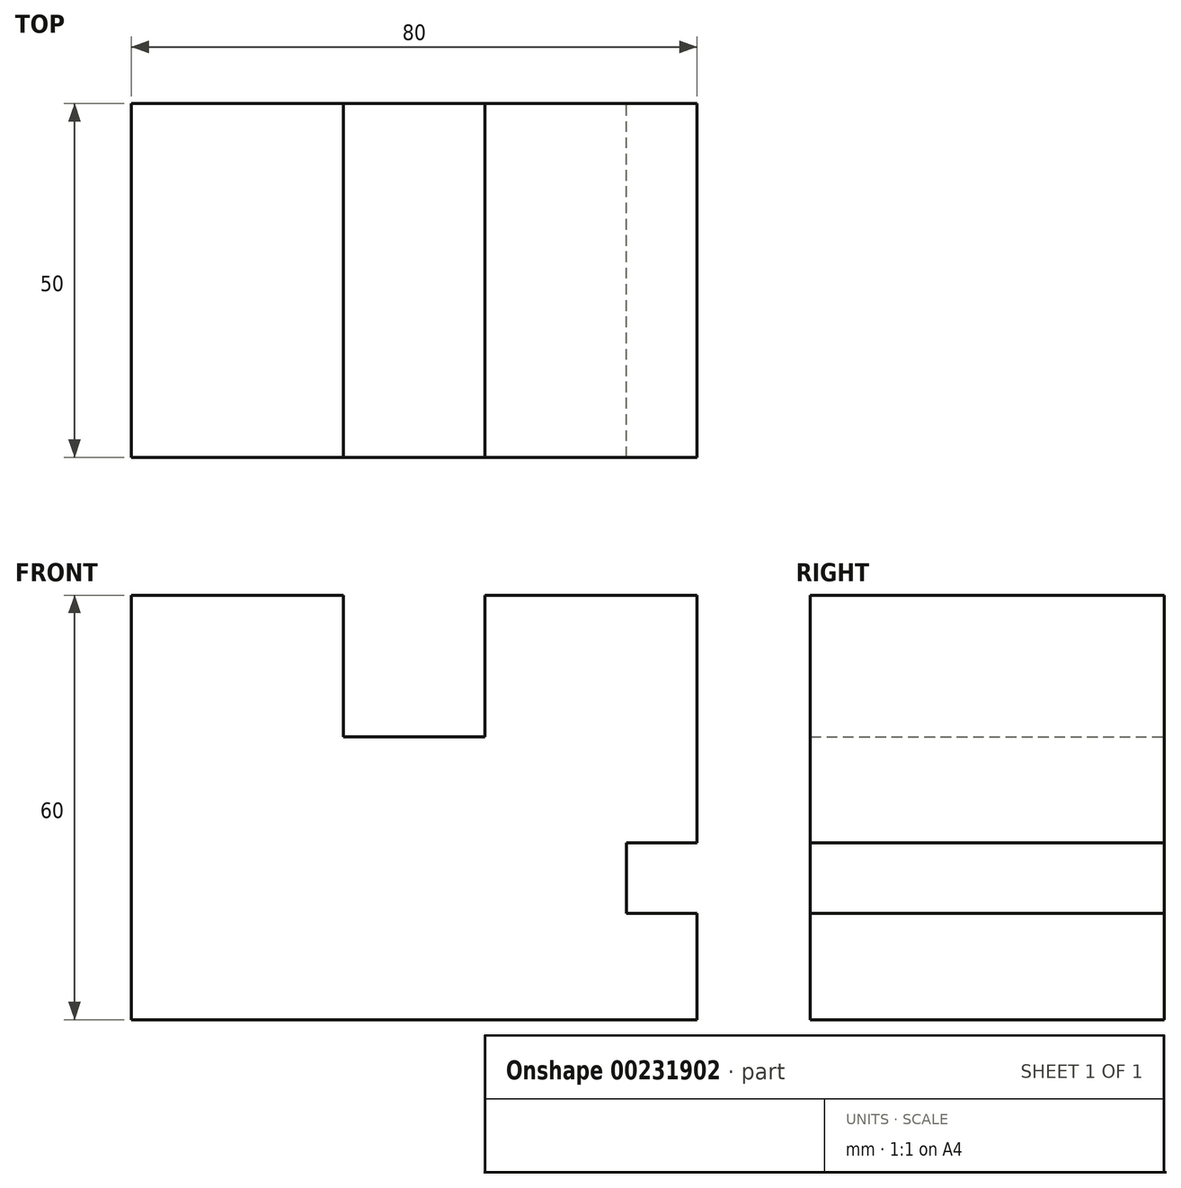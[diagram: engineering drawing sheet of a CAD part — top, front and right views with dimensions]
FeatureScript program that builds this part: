
annotation { "Feature Type Name" : "Feature", "Feature Type Description" : "" }
export const myFeature = defineFeature(function(context is Context, id is Id, definition is map)
    precondition{}
    {
        {
            var Q0;
            Q0=qCreatedBy(makeId("Front.planeOp"),FACE);
            var sketch = newSketch(context, id + "F0", { "sketchPlane" : qUnion([Q0])});
            skLineSegment(sketch, "E0", {"start": v(-80, 60) * mm, "end": v(-50, 60) * mm});
            skLineSegment(sketch, "E1", {"start": v(-50, 60) * mm, "end": v(-50, 40) * mm});
            skLineSegment(sketch, "E2", {"start": v(-50, 40) * mm, "end": v(-30, 40) * mm});
            skLineSegment(sketch, "E3", {"start": v(-30, 40) * mm, "end": v(-30, 60) * mm});
            skLineSegment(sketch, "E4", {"start": v(-30, 60) * mm, "end": v(0, 60) * mm});
            skLineSegment(sketch, "E5", {"start": v(0, 60) * mm, "end": v(0, 25) * mm});
            skLineSegment(sketch, "E6", {"start": v(0, 25) * mm, "end": v(-10, 25) * mm});
            skLineSegment(sketch, "E7", {"start": v(-10, 25) * mm, "end": v(-10, 15) * mm});
            skLineSegment(sketch, "E8", {"start": v(-10, 15) * mm, "end": v(0, 15) * mm});
            skLineSegment(sketch, "E9", {"start": v(0, 15) * mm, "end": v(0, 0) * mm});
            skLineSegment(sketch, "E10", {"start": v(0, 0) * mm, "end": v(-80, 0) * mm});
            skLineSegment(sketch, "E11", {"start": v(-80, 0) * mm, "end": v(-80, 60) * mm});
            skSolve(sketch);
        }
        {
            var Q0;
            Q0=makeQuery(id+"F0.imprint","IMPRINT",FACE,{"disambiguationData":[TD([[makeQuery(id+"F0.imprint","IMPRINT",EDGE,{"derivedFrom":sQuery(id+"F0.wireOp",EDGE,"E0")}),-1.0]])]});
            extrude(context, id + "F1", {"entities" : qUnion([Q0]), "depth" : 50 * mm});
        }
    });
